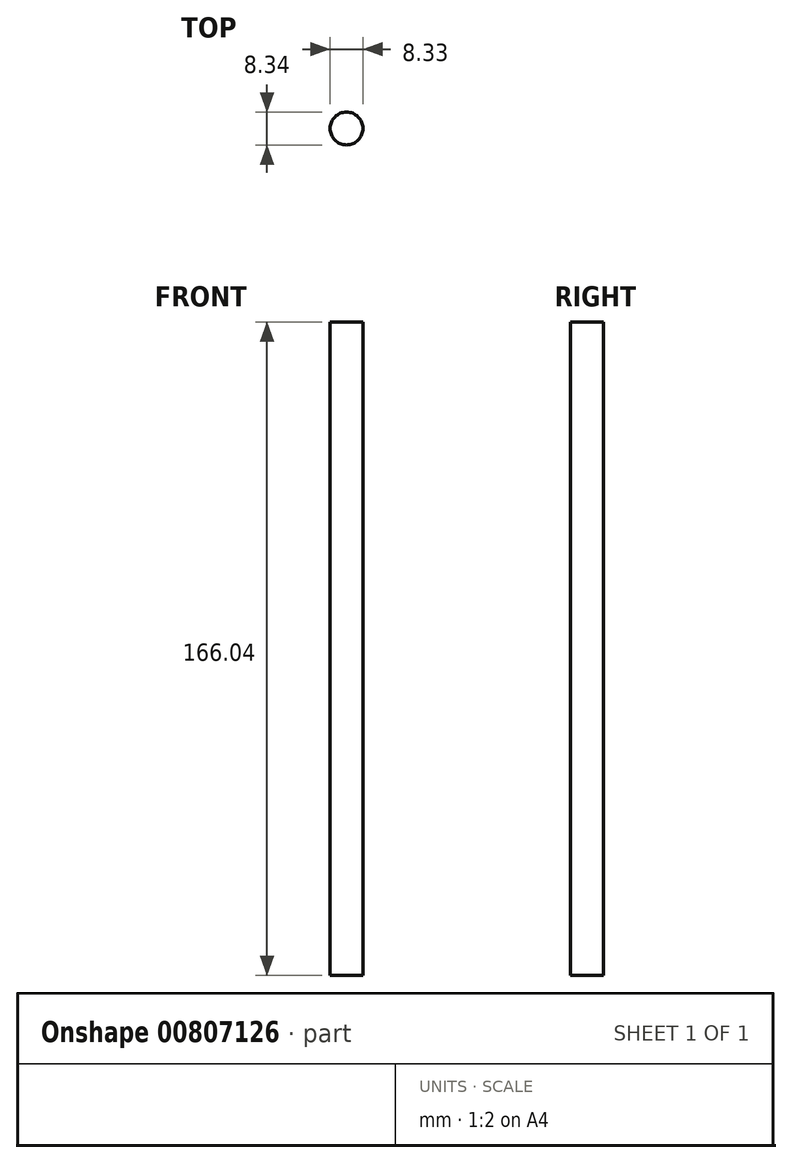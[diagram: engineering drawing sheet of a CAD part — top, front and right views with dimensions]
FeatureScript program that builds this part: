
annotation { "Feature Type Name" : "Feature", "Feature Type Description" : "" }
export const myFeature = defineFeature(function(context is Context, id is Id, definition is map)
    precondition{}
    {
        {
            var Q0;
            Q0=qCreatedBy(makeId("Front.planeOp"),FACE);
            var sketch = newSketch(context, id + "F0", { "sketchPlane" : qUnion([Q0])});
            skFitSpline(sketch, "E0", {"points": [v(0, 0) * mm, v(-16.96, 12.2) * mm, v(-37.2, 25.89) * mm, v(-26.48, 40.17) * mm, v(-4.17, 47.31) * mm, v(4.46, 61.3) * mm, v(8.03, 66.66) * mm, v(11.01, 38.39) * mm, v(-17.26, 28.27) * mm, v(-3.87, 11.3) * mm, v(6.25, 2.98) * mm, v(0, 0) * mm]});
            skLineSegment(sketch, "E1", {"start": v(0, 78.26) * mm, "end": v(0, -20.23) * mm});
            skSolve(sketch);
        }
        {
            var Q0;
            Q0=qCreatedBy(makeId("Front.planeOp"),FACE);
            var sketch = newSketch(context, id + "F1", { "sketchPlane" : qUnion([Q0])});
            skFitSpline(sketch, "E2", {"points": [v(2.08, 0) * mm, v(-15.18, 8.93) * mm, v(-17.56, 37.2) * mm, v(-24.4, 40.77) * mm, v(-38.09, 47.02) * mm, v(-39.87, 62.5) * mm, v(-41.66, 51.48) * mm, v(-38.98, 41.36) * mm, v(-25, 37.5) * mm, v(-20.23, 25) * mm, v(-18.75, 8.33) * mm, v(-12.8, 0) * mm, v(2.08, 0) * mm]});
            skLineSegment(sketch, "E3", {"start": v(0, 79.45) * mm, "end": v(0, -83.92) * mm});
            skSolve(sketch);
        }
        {
            var Q0;
            {var subQ0=sQuery(id+"F1.wireOp",EDGE,"E3");var subQ1=sQuery(id+"F1.wireOp",EDGE,"E2");var subQ2=makeQuery(id+"F1.imprint","INTERSECT",VERTEX,{"disambiguationData":[OD(0.0)],"derivedFrom":[subQ1,subQ0]});Q0=makeQuery(id+"F1.imprint","IMPRINT",FACE,{"disambiguationData":[TD([[makeQuery(id+"F1.imprint","IMPRINT",EDGE,{"disambiguationData":[TD([[subQ2,1.0]])],"derivedFrom":subQ1}),1.0]])]});}
            var Q1;
            Q1=sQuery(id+"F1.wireOp",EDGE,"E3");
            revolve(context, id + "F2", {"surfaceOperationType" : NewSurfaceOperationType.NEW, "entities" : qUnion([Q0]), "axis" : qUnion([Q1]), "revolveType" : RevolveType.FULL});
        }
        {
            var Q0;
            Q0=qCreatedBy(makeId("Front.planeOp"),FACE);
            var sketch = newSketch(context, id + "F3", { "sketchPlane" : qUnion([Q0])});
            skLineSegment(sketch, "E4", {"start": v(3.27, -2.38) * mm, "end": v(3.27, -162.47) * mm});
            skLineSegment(sketch, "E5", {"start": v(3.27, -162.47) * mm, "end": v(-0.9, -162.47) * mm});
            skLineSegment(sketch, "E6", {"start": v(-0.9, -162.47) * mm, "end": v(-0.9, -3.27) * mm});
            skLineSegment(sketch, "E7", {"start": v(-0.9, -3.27) * mm, "end": v(-0.9, 3.57) * mm});
            skLineSegment(sketch, "E8", {"start": v(-0.9, 3.57) * mm, "end": v(3.27, 3.57) * mm});
            skLineSegment(sketch, "E9", {"start": v(3.27, 3.57) * mm, "end": v(3.27, -2.38) * mm});
            skSolve(sketch);
        }
        {
            var Q0;
            Q0=makeQuery(id+"F3.imprint","IMPRINT",FACE,{"disambiguationData":[TD([[makeQuery(id+"F3.imprint","IMPRINT",EDGE,{"derivedFrom":sQuery(id+"F3.wireOp",EDGE,"E4")}),-1.0]])]});
            var Q1;
            Q1=sQuery(id+"F3.wireOp",EDGE,"E6");
            revolve(context, id + "F4", {"operationType" : NewBodyOperationType.ADD, "surfaceOperationType" : NewSurfaceOperationType.NEW, "entities" : qUnion([Q0]), "axis" : qUnion([Q1]), "revolveType" : RevolveType.FULL});
        }
    });
